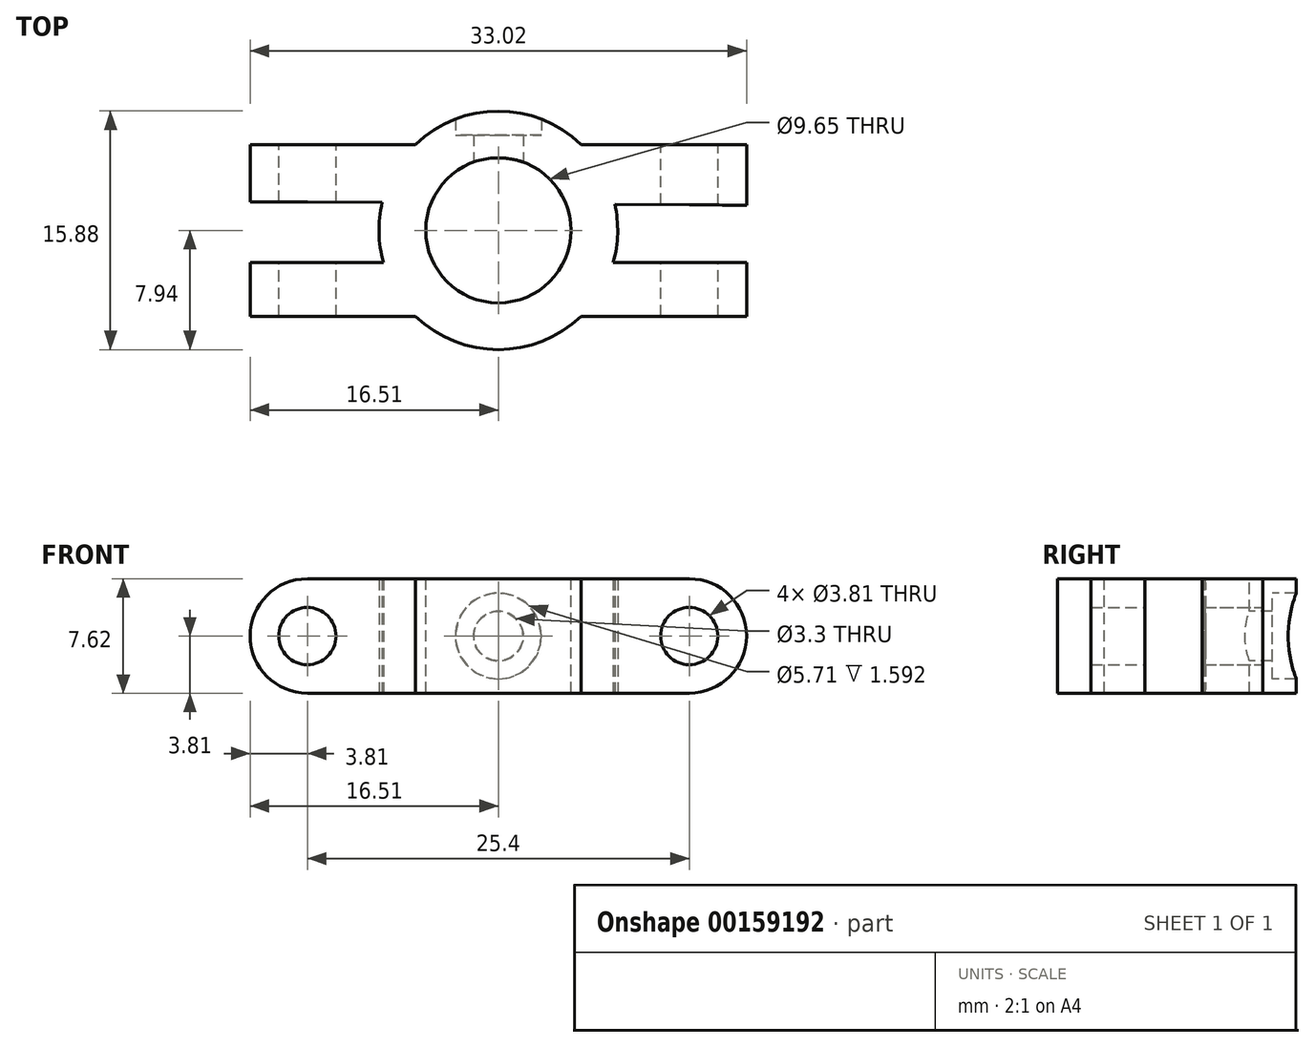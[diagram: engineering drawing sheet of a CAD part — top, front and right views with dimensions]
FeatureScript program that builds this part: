
annotation { "Feature Type Name" : "Feature", "Feature Type Description" : "" }
export const myFeature = defineFeature(function(context is Context, id is Id, definition is map)
    precondition{}
    {
        {
            var Q0;
            Q0=qCreatedBy(makeId("Top.planeOp"),FACE);
            var sketch = newSketch(context, id + "F0", { "sketchPlane" : qUnion([Q0])});
            skLineSegment(sketch, "E0", {"start": v(0, 0) * mm, "end": v(12.7, 0) * mm});
            skLineSegment(sketch, "E1", {"start": v(0, 0) * mm, "end": v(0, -5.72) * mm});
            skLineSegment(sketch, "E2", {"start": v(0, -5.72) * mm, "end": v(16.51, -5.72) * mm});
            skLineSegment(sketch, "E3", {"start": v(16.51, -5.72) * mm, "end": v(16.51, 5.72) * mm});
            skLineSegment(sketch, "E4", {"start": v(16.51, 5.72) * mm, "end": v(-16.51, 5.72) * mm});
            skLineSegment(sketch, "E5", {"start": v(-16.51, 5.72) * mm, "end": v(-16.51, -5.72) * mm});
            skLineSegment(sketch, "E6", {"start": v(-16.51, -5.72) * mm, "end": v(0, -5.72) * mm});
            skSolve(sketch);
        }
        {
            var Q0;
            Q0 = qSketchRegion(id + "F0", true);
            extrude(context, id + "F1", {"entities" : qUnion([Q0]), "depth" : 7.62 * mm});
        }
        {
            var Q0;
            Q0=makeQuery(id+"F1.opExtrude","CAP_FACE",FACE,{"disambiguationData":[OSD([sQuery(id+"F0.wireOp",EDGE,"E2"),sQuery(id+"F0.wireOp",EDGE,"E3"),sQuery(id+"F0.wireOp",EDGE,"E4"),sQuery(id+"F0.wireOp",EDGE,"E5"),sQuery(id+"F0.wireOp",EDGE,"E6")])],"isStart":false});
            var sketch = newSketch(context, id + "F2", { "sketchPlane" : qUnion([Q0])});
            skLineSegment(sketch, "E7", {"start": v(-16.51, 0) * mm, "end": v(-16.51, 1.9) * mm});
            skLineSegment(sketch, "E8", {"start": v(-16.51, 1.9) * mm, "end": v(16.51, 1.67) * mm});
            skLineSegment(sketch, "E9", {"start": v(16.51, 1.67) * mm, "end": v(16.51, -2.14) * mm});
            skLineSegment(sketch, "E10", {"start": v(16.51, -2.14) * mm, "end": v(-16.51, -2.14) * mm});
            skLineSegment(sketch, "E11", {"start": v(-16.51, -2.14) * mm, "end": v(-16.51, 0) * mm});
            skSolve(sketch);
        }
        {
            var Q0;
            Q0 = qSketchRegion(id + "F2", true);
            extrude(context, id + "F3", {"entities" : qUnion([Q0]), "operationType" : NewBodyOperationType.REMOVE, "oppositeDirection" : true, "depth" : 7.62 * mm});
        }
        {
            var Q0;
            Q0=makeQuery(id+"F1.opExtrude","SWEPT_FACE",FACE,{"disambiguationData":[OSD([sQuery(id+"F0.wireOp",EDGE,"E4")])]});
            var sketch = newSketch(context, id + "F4", { "sketchPlane" : qUnion([Q0])});
            skLineSegment(sketch, "E12", {"start": v(16.51, 3.81) * mm, "end": v(12.7, 3.81) * mm});
            skArc(sketch, "E13", {"start": v(12.7, 7.62) * mm, "mid": v(16.51, 3.81) * mm, "end": v(12.7, 0) * mm});
            skLineSegment(sketch, "E14", {"start": v(12.7, 0) * mm, "end": v(16.51, 0) * mm});
            skLineSegment(sketch, "E15", {"start": v(16.51, 0) * mm, "end": v(16.51, 7.62) * mm});
            skLineSegment(sketch, "E16", {"start": v(16.51, 7.62) * mm, "end": v(12.7, 7.62) * mm});
            skLineSegment(sketch, "E17", {"start": v(-16.51, 3.81) * mm, "end": v(-12.7, 3.81) * mm});
            skPoint(sketch, "E17.endSnap0", {"position": v(-16.51, 3.81) * mm});
            skArc(sketch, "E18", {"start": v(-12.7, 0) * mm, "mid": v(-16.51, 3.8) * mm, "end": v(-12.7, 7.62) * mm});
            skLineSegment(sketch, "E19", {"start": v(-12.7, 7.62) * mm, "end": v(-16.51, 7.62) * mm});
            skLineSegment(sketch, "E20", {"start": v(-16.51, 7.62) * mm, "end": v(-16.51, 0) * mm});
            skLineSegment(sketch, "E21", {"start": v(-16.51, 0) * mm, "end": v(-12.7, 0) * mm});
            skCircle(sketch, "E22", {"center": v(-12.7, 3.81) * mm, "radius": 1.9 * mm});
            skCircle(sketch, "E23", {"center": v(12.7, 3.81) * mm, "radius": 1.9 * mm});
            skSolve(sketch);
        }
        {
            var Q0;
            Q0 = qSketchRegion(id + "F4", true);
            extrude(context, id + "F5", {"entities" : qUnion([Q0]), "operationType" : NewBodyOperationType.REMOVE, "endBound" : BoundingType.THROUGH_ALL, "oppositeDirection" : true, "depth" : 25.4 * mm});
        }
        {
            var Q0;
            Q0=qCreatedBy(makeId("Top.planeOp"),FACE);
            var sketch = newSketch(context, id + "F6", { "sketchPlane" : qUnion([Q0])});
            skCircle(sketch, "E24", {"center": v(0, 0) * mm, "radius": 7.94 * mm});
            skSolve(sketch);
        }
        {
            var Q0;
            Q0 = qSketchRegion(id + "F6", true);
            var Q1;
            {var subQ0=sQuery(id+"F0.wireOp",EDGE,"E6");var subQ1=sQuery(id+"F0.wireOp",EDGE,"E2");var subQ2=sQuery(id+"F0.wireOp",EDGE,"E3");var subQ3=sQuery(id+"F0.wireOp",EDGE,"E5");Q1=makeQuery(id+"F3.boolean.opBoolean","SPLIT",FACE,{"disambiguationData":[TD([makeQuery(id+"F3.opExtrude","SWEPT_FACE",FACE,{"disambiguationData":[OSD([sQuery(id+"F2.wireOp",EDGE,"E10")])]})])],"derivedFrom":makeQuery(id+"F1.opExtrude","CAP_FACE",FACE,{"disambiguationData":[OSD([subQ1,subQ2,sQuery(id+"F0.wireOp",EDGE,"E4"),subQ3,subQ0])],"isStart":false})});}
            extrude(context, id + "F7", {"entities" : qUnion([Q0]), "operationType" : NewBodyOperationType.ADD, "endBound" : BoundingType.UP_TO_SURFACE, "endBoundEntityFace" : qUnion([Q1]), "depth" : 7.62 * mm});
        }
        {
            var Q0;
            {var subQ0=sQuery(id+"F0.wireOp",EDGE,"E6");var subQ1=sQuery(id+"F0.wireOp",EDGE,"E5");var subQ2=sQuery(id+"F0.wireOp",EDGE,"E4");var subQ3=sQuery(id+"F0.wireOp",EDGE,"E3");var subQ4=sQuery(id+"F0.wireOp",EDGE,"E2");var subQ7=makeQuery(id+"F1.opExtrude","CAP_FACE",FACE,{"disambiguationData":[OSD([subQ4,subQ3,subQ2,subQ1,subQ0])],"isStart":false});Q0=makeQuery(id+"F7.boolean.opBoolean","MERGE",FACE,{"derivedFrom":[makeQuery(id+"F3.boolean.opBoolean","SPLIT",FACE,{"disambiguationData":[TD([makeQuery(id+"F3.opExtrude","SWEPT_FACE",FACE,{"disambiguationData":[OSD([sQuery(id+"F2.wireOp",EDGE,"E10")])]})])],"derivedFrom":subQ7}),makeQuery(id+"F3.boolean.opBoolean","SPLIT",FACE,{"disambiguationData":[TD([makeQuery(id+"F1.opExtrude","SWEPT_FACE",FACE,{"disambiguationData":[OSD([subQ2])]})])],"derivedFrom":subQ7}),makeQuery(id+"F7.opExtrude","CAP_FACE",FACE,{"disambiguationData":[OSD([subQ4,subQ3,subQ2,subQ1,subQ0])],"isStart":false})]});}
            var sketch = newSketch(context, id + "F8", { "sketchPlane" : qUnion([Q0])});
            skCircle(sketch, "E25", {"center": v(0, 0) * mm, "radius": 4.83 * mm});
            skSolve(sketch);
        }
        {
            var Q0;
            Q0 = qSketchRegion(id + "F8", true);
            extrude(context, id + "F9", {"entities" : qUnion([Q0]), "operationType" : NewBodyOperationType.REMOVE, "oppositeDirection" : true, "depth" : 25.4 * mm});
        }
        {
            var Q0;
            Q0=qCreatedBy(makeId("Front.planeOp"),FACE);
            var sketch = newSketch(context, id + "F10", { "sketchPlane" : qUnion([Q0])});
            skLineSegment(sketch, "E26", {"start": v(0, 0) * mm, "end": v(0, 3.81) * mm});
            skCircle(sketch, "E27", {"center": v(0, 3.81) * mm, "radius": 1.65 * mm});
            skSolve(sketch);
        }
        {
            var Q0;
            Q0 = qSketchRegion(id + "F10", true);
            extrude(context, id + "F11", {"entities" : qUnion([Q0]), "operationType" : NewBodyOperationType.REMOVE, "oppositeDirection" : true, "depth" : 25.4 * mm});
        }
        {
            var Q0;
            Q0=qCreatedBy(makeId("Front.planeOp"),FACE);
            cPlane(context, id + "F12", {"entities" : qUnion([Q0]), "cplaneType" : CPlaneType.OFFSET, "offset" : 6.35 * mm, "oppositeDirection" : true, "width" : 152.4 * mm, "height" : 152.4 * mm});
        }
        {
            var Q0;
            Q0=qCreatedBy(id+"F12.planeOp",FACE);
            var sketch = newSketch(context, id + "F13", { "sketchPlane" : qUnion([Q0])});
            skLineSegment(sketch, "E28", {"start": v(0, 0) * mm, "end": v(0, 3.81) * mm});
            skCircle(sketch, "E29", {"center": v(0, 3.81) * mm, "radius": 2.86 * mm});
            skSolve(sketch);
        }
        {
            var Q0;
            Q0 = qSketchRegion(id + "F13", true);
            extrude(context, id + "F14", {"entities" : qUnion([Q0]), "operationType" : NewBodyOperationType.REMOVE, "oppositeDirection" : true, "depth" : 25.4 * mm});
        }
    });
